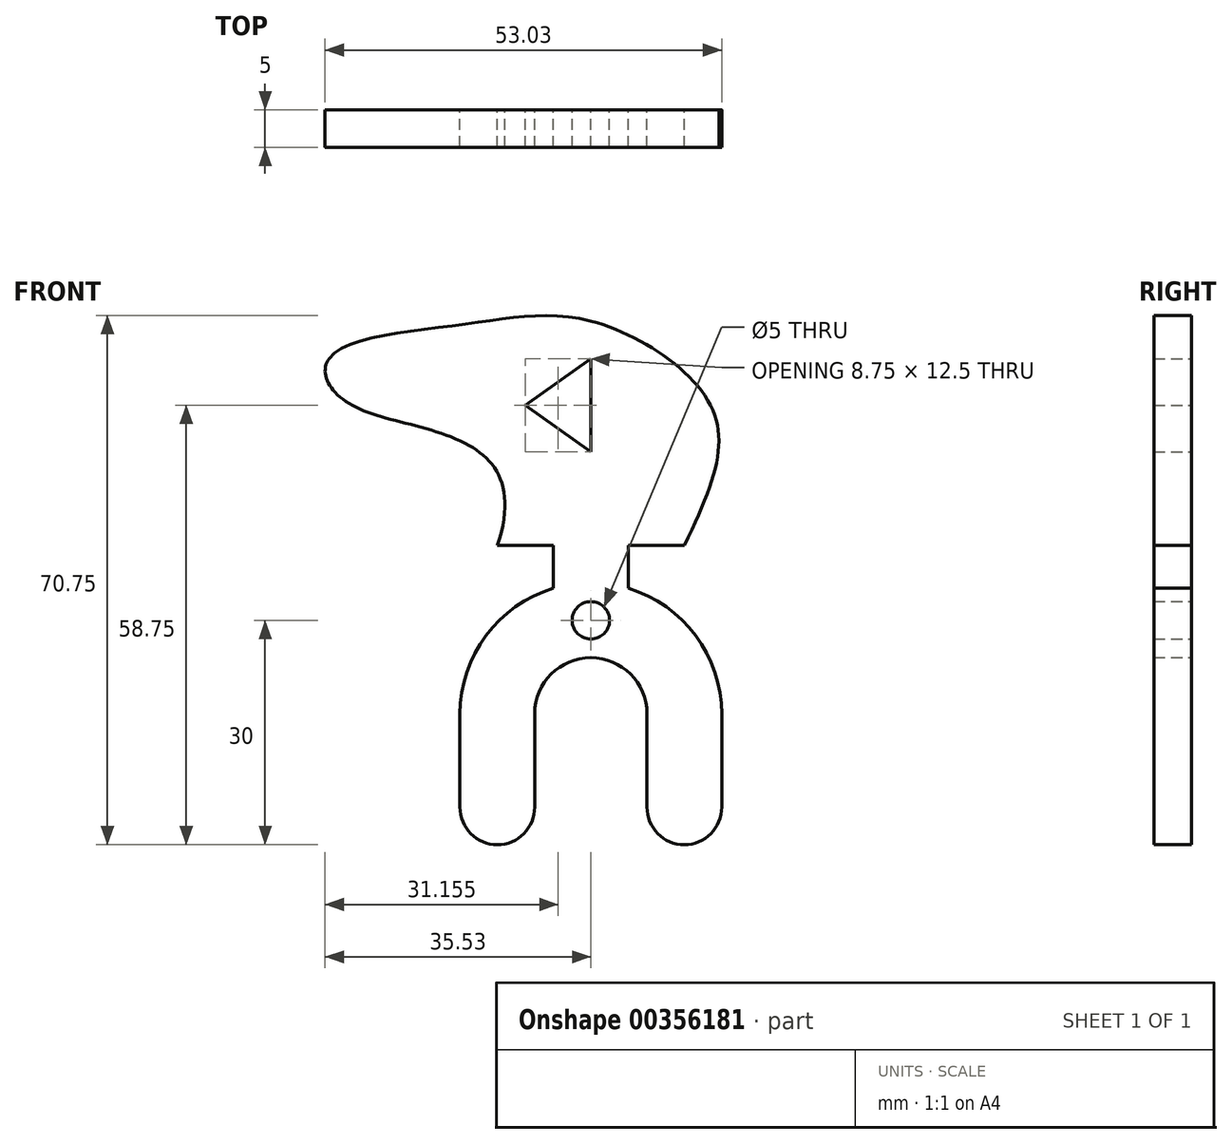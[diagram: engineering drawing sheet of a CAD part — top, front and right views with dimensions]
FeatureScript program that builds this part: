
annotation { "Feature Type Name" : "Feature", "Feature Type Description" : "" }
export const myFeature = defineFeature(function(context is Context, id is Id, definition is map)
    precondition{}
    {
        {
            var Q0;
            Q0=qCreatedBy(makeId("Front.planeOp"),FACE);
            var sketch = newSketch(context, id + "F0", { "sketchPlane" : qUnion([Q0])});
            skLineSegment(sketch, "E0.bottom", {"start": v(-17.5, 0) * mm, "end": v(-7.5, 0) * mm});
            skLineSegment(sketch, "E0.top", {"start": v(-17.5, -12.5) * mm, "end": v(-7.5, -12.5) * mm});
            skLineSegment(sketch, "E0.left", {"start": v(-17.5, 0) * mm, "end": v(-17.5, -12.5) * mm});
            skLineSegment(sketch, "E0.right", {"start": v(-7.5, 0) * mm, "end": v(-7.5, -12.5) * mm});
            skLineSegment(sketch, "E1.bottom", {"start": v(7.5, 0) * mm, "end": v(17.5, 0) * mm});
            skLineSegment(sketch, "E1.top", {"start": v(7.5, -12.5) * mm, "end": v(17.5, -12.5) * mm});
            skLineSegment(sketch, "E1.left", {"start": v(7.5, 0) * mm, "end": v(7.5, -12.5) * mm});
            skLineSegment(sketch, "E1.right", {"start": v(17.5, 0) * mm, "end": v(17.5, -12.5) * mm});
            skArc(sketch, "E2", {"start": v(-7.5, 0) * mm, "mid": v(0, 7.5) * mm, "end": v(7.5, 0) * mm});
            skArc(sketch, "E3", {"start": v(-7.5, -12.5) * mm, "mid": v(-12.5, -17.5) * mm, "end": v(-17.5, -12.5) * mm});
            skArc(sketch, "E4", {"start": v(7.5, -12.5) * mm, "mid": v(12.5, -17.5) * mm, "end": v(17.5, -12.5) * mm});
            skArc(sketch, "E5", {"start": v(8.4, -15.35) * mm, "mid": v(0, 17.5) * mm, "end": v(-8.4, -15.35) * mm});
            skPoint(sketch, "E6", {"position": v(0, 17.5) * mm});
            skPoint(sketch, "E7", {"position": v(0, -12.5) * mm});
            skLineSegment(sketch, "E8", {"start": v(0, 7.5) * mm, "end": v(0, 17.5) * mm});
            skPoint(sketch, "E9", {"position": v(0, 12.5) * mm});
            skCircle(sketch, "E10", {"center": v(0, 12.5) * mm, "radius": 2.5 * mm});
            skLineSegment(sketch, "E11.bottom", {"start": v(-5, 32.5) * mm, "end": v(5, 32.5) * mm});
            skLineSegment(sketch, "E11.top", {"start": v(-5, 7.5) * mm, "end": v(5, 7.5) * mm});
            skLineSegment(sketch, "E11.left", {"start": v(-5, 32.5) * mm, "end": v(-5, 7.5) * mm});
            skLineSegment(sketch, "E11.right", {"start": v(5, 32.5) * mm, "end": v(5, 7.5) * mm});
            skPoint(sketch, "E12", {"position": v(0, 7.5) * mm});
            skLineSegment(sketch, "E13", {"start": v(0, 17.5) * mm, "end": v(0, 32.5) * mm});
            skPoint(sketch, "E14", {"position": v(0, 22.5) * mm});
            skLineSegment(sketch, "E15", {"start": v(-12.5, 22.5) * mm, "end": v(12.5, 22.5) * mm});
            skLineSegment(sketch, "E16", {"start": v(0, 22.5) * mm, "end": v(0, 47.5) * mm});
            skPoint(sketch, "E17", {"position": v(0, 35) * mm});
            skLineSegment(sketch, "E18", {"start": v(0, 35) * mm, "end": v(0, 47.5) * mm});
            skPoint(sketch, "E19", {"position": v(0, 41.25) * mm});
            skFitSpline(sketch, "E20", {"points": [v(12.5, 22.5) * mm, v(16, 41.25) * mm, v(0, 52.5) * mm, v(-17.5, 52) * mm, v(-35, 47.5) * mm, v(-30.88, 40.72) * mm, v(-12.5, 22.5) * mm], "startDerivative": vector(69.6, 144.37) * mm, "endDerivative": vector(-77.1, -231.37) * mm});
            skLineSegment(sketch, "E21", {"start": v(-35, 47.5) * mm, "end": v(0, 47.5) * mm});
            skLineSegment(sketch, "E22", {"start": v(0, 41.25) * mm, "end": v(16, 41.25) * mm});
            skLineSegment(sketch, "E23", {"start": v(0, 47.5) * mm, "end": v(0, 52.5) * mm});
            skPoint(sketch, "E24", {"position": v(-17.5, 47.5) * mm});
            skLineSegment(sketch, "E25", {"start": v(-17.5, 47.5) * mm, "end": v(0, 35) * mm});
            skLineSegment(sketch, "E26", {"start": v(0, 47.5) * mm, "end": v(-8.75, 41.25) * mm});
            skLineSegment(sketch, "E27", {"start": v(0, 47.5) * mm, "end": v(-16.27, 35.88) * mm});
            skLineSegment(sketch, "E28", {"start": v(-35, 47.5) * mm, "end": v(-30.88, 40.72) * mm});
            skLineSegment(sketch, "E29", {"start": v(-17.5, 47.5) * mm, "end": v(-30.88, 40.72) * mm});
            skLineSegment(sketch, "E30", {"start": v(-30.88, 40.72) * mm, "end": v(-30.88, 47.5) * mm});
            skSolve(sketch);
        }
        {
            var Q0;
            Q0 = qSketchRegion(id + "F0", true);
            var Q1;
            {var subQ0=sQuery(id+"F0.wireOp",EDGE,"E27");var subQ3=sQuery(id+"F0.wireOp",EDGE,"E25");var subQ5=makeQuery(id+"F0.imprint","INTERSECT",VERTEX,{"derivedFrom":[subQ3,subQ0]});Q1=makeQuery(id+"F0.imprint","IMPRINT",FACE,{"disambiguationData":[TD([[makeQuery(id+"F0.imprint","IMPRINT",EDGE,{"disambiguationData":[TD([[subQ5,1.0]])],"derivedFrom":subQ3}),1.0]])]});}
            var Q2;
            {var subQ1=sQuery(id+"F0.wireOp",EDGE,"E18");var subQ3=makeQuery(id+"F0.imprint","INTERSECT",VERTEX,{"derivedFrom":[subQ1,sQuery(id+"F0.wireOp",EDGE,"E22")]});Q2=makeQuery(id+"F0.imprint","IMPRINT",FACE,{"disambiguationData":[TD([[makeQuery(id+"F0.imprint","IMPRINT",EDGE,{"disambiguationData":[TD([[subQ3,1.0]])],"derivedFrom":subQ1}),1.0]])]});}
            extrude(context, id + "F1", {"entities" : qUnion([Q0, Q1, Q2]), "depth" : 5 * mm});
        }
    });
